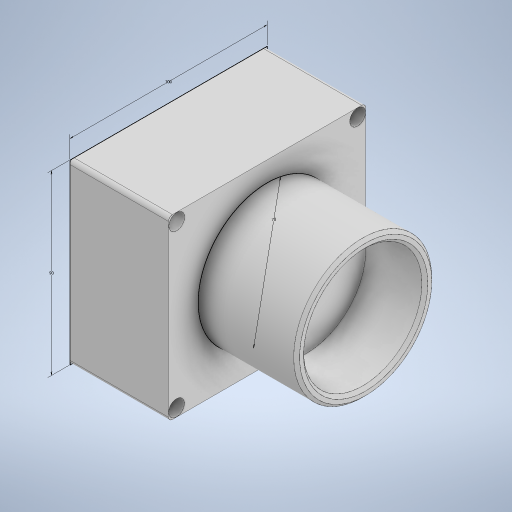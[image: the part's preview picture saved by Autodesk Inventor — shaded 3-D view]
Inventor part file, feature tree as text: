
AUTODESK INVENTOR PART (.ipt)
format: ipt  version: 2024 (Build 280153000, 153)  size: 296,448 bytes
history: native  units: mm
features: sketch x8, hole x4, extrude x3, other x1, chamfer x1, fillet x1
ambient origin geometry x8: Origin, YZ Plane, XZ Plane, XY Plane, X Axis, Y Axis, Z Axis, Center Point
bodies: Body1 (feature_tree)
feature tree (18):
  other  "Sólido1"
  sketch  "Boceto1"  dims[d0=90.0mm d1=100.0mm]
  extrude  "Extrusión1"  Depth=100.0mm
  sketch  "Boceto2"  dims[d2=50.0mm d3=0.0mm d4=70.0mm]
  extrude  "Extrusión2"  Depth=70.0mm
  extrude  "Extrusión3"  Depth=30.0mm
  chamfer  "Chaflán1"  Distance=30.0mm
  sketch  "Boceto4"  dims[d10=1.5mm d11=2.0mm d12=45.0deg d13=2.0mm]
  fillet  "Empalme1"  Radius=2.0mm
  hole  "Agujero1"  [1 undecoded]
  hole  "Agujero2"  [1 undecoded]
  hole  "Agujero3"  [1 undecoded]
  hole  "Agujero4"  [1 undecoded]
  sketch  "Boceto3"  dims[d5=50.0mm d6=0.0mm d7=60.0mm d8=30.0mm d9=0.0mm]
  sketch  "Boceto5"  dims[d14=8.0mm d15=6.0mm d16=4.0mm d17=2.0mm d18=90.0deg d19=8.0mm d20=20.594885mm d21=4.1mm]
  sketch  "Boceto6"  dims[d22=8.0mm d23=6.0mm d24=4.0mm d25=2.0mm d26=90.0deg d27=8.0mm d28=20.594885mm d29=4.1mm]
  sketch  "Boceto7"  dims[d30=8.0mm d31=6.0mm d32=4.0mm d33=2.0mm d34=90.0deg d35=8.0mm d36=20.594885mm d37=4.1mm]
  sketch  "Boceto8"  dims[d38=8.0mm d39=6.0mm d40=4.0mm d41=2.0mm d42=90.0deg d43=8.0mm d44=20.594885mm]
note: 4 required parameter values undecoded (feature->parameter linkage not recoverable at this tier; creation-order binding heuristic only, values carry confidence <= 0.55)
